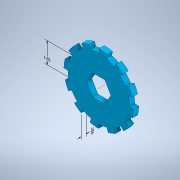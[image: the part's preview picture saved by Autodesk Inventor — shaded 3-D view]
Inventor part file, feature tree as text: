
AUTODESK INVENTOR PART (.ipt)
format: ipt  version: 2022.2 (Build 262287000, 287)  size: 702,976 bytes
history: native  units: in
note: dims shown in document units (in); Inventor stores cm internally (conversion verified against a paired STEP export)
features: sketch x4, other x3, extrude x3, pattern_circular x1, emboss x1
ambient origin geometry x8: Origin, YZ Plane, XZ Plane, XY Plane, X Axis, Y Axis, Z Axis, Center Point
bodies: Solid1 (feature_tree)
feature tree (12):
  other  "Annotations"
  extrude  "Extrusion1"  Depth=0.25in TaperAngle=0.0deg
  extrude  "Extrusion11"  TaperAngle=0.0deg  [1 undecoded]
  extrude  "Extrusion19"  Depth=0.0034in
  pattern_circular  "Circular Pattern11"  [2 undecoded]
  emboss  "Emboss1"
  sketch  "Sketch1"  dims[d0=2.985in d1=0.25in d2=0.0in]
  sketch  "Sketch10"  dims[d55=1.015in d56=0.0in d57=0.0in]
  sketch  "Sketch17"  dims[d123=0.1963in d124=0.0034in]
  sketch  "Sketch35"  dims[d125=0.0962in d126=0.25in d127=0.0in d128=4.7244in d129=360.0deg d131=2.985in d132=3.3777in d212=2.0in d213=0.1in d214=0.0in d136=0.25in d209=0.2158in d210=0.2107in d211=1.015in]
  other  "Linear Dimension 2"
  other  "Linear Dimension 3"
note: 3 required parameter values undecoded (feature->parameter linkage not recoverable at this tier; creation-order binding heuristic only, values carry confidence <= 0.55)
